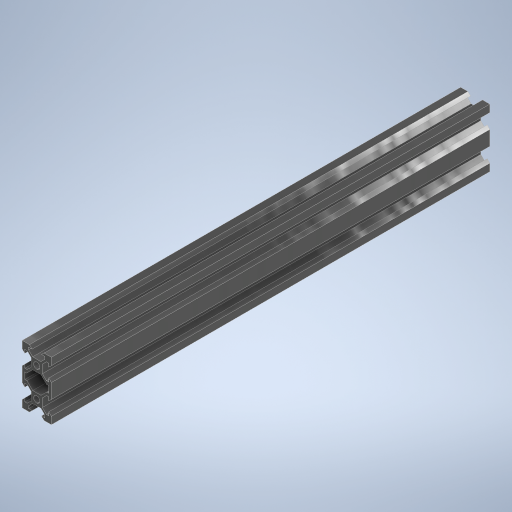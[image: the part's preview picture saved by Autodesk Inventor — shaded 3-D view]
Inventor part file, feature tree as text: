
AUTODESK INVENTOR PART (.ipt)
format: ipt  version: 2024.2 (Build 282272000, 272)  size: 413,696 bytes
history: native  units: mm
features: extrude x2, sketch x2, pattern_linear x1
ambient origin geometry x8: Origin, YZ Plane, XZ Plane, XY Plane, X Axis, Y Axis, Z Axis, Center Point
bodies: Solid1 (feature_tree)
feature tree (5):
  extrude  "Extrusion1"  Depth=10.0mm
  pattern_linear  "Rectangular Pattern1"  Spacing1=4.4mm  [1 undecoded]
  extrude  "Extrusion2"  TaperAngle=45.0deg  [1 undecoded]
  sketch  "Sketch1"  dims[d16=10.0mm d19=3.2mm]
  sketch  "Sketch2"  dims[d21=4.4mm d22=4.4mm d24=45.0deg d25=1.8mm d27=1.8mm d28=45.0deg d29=3.2mm d31=1.4mm d33=2.15mm d34=3.825mm d35=3.825mm d36=135.0deg d37=40.0mm d39=360.0deg d41=300.0mm d42=0.0mm d43=20.0mm d45=20.0mm d46=4.5mm d48=0.0mm d49=0.0mm d50=1.8mm d51=0.5mm d52=0.872665mm d53=0.5mm d54=0.872665mm]
note: 2 required parameter values undecoded (feature->parameter linkage not recoverable at this tier; creation-order binding heuristic only, values carry confidence <= 0.55)
